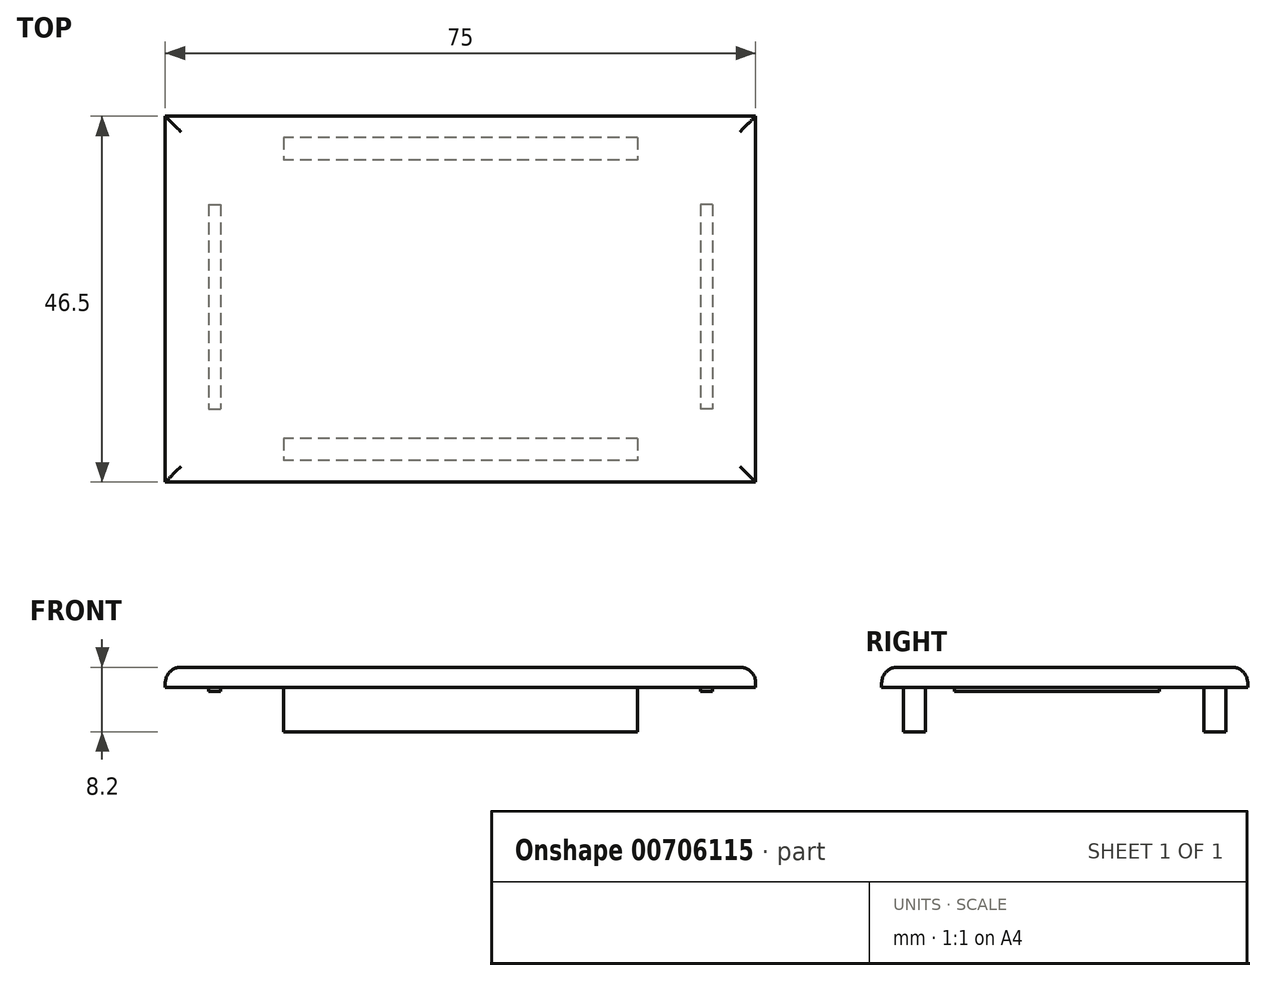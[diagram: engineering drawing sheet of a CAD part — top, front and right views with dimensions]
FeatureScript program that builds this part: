
annotation { "Feature Type Name" : "Feature", "Feature Type Description" : "" }
export const myFeature = defineFeature(function(context is Context, id is Id, definition is map)
    precondition{}
    {
        {
            var Q0;
            Q0=qCreatedBy(makeId("Top.planeOp"),FACE);
            var sketch = newSketch(context, id + "F0", { "sketchPlane" : qUnion([Q0])});
            skLineSegment(sketch, "E0.bottom", {"start": v(37.5, -23.25) * mm, "end": v(-37.5, -23.25) * mm});
            skLineSegment(sketch, "E0.top", {"start": v(37.5, 23.25) * mm, "end": v(-37.5, 23.25) * mm});
            skLineSegment(sketch, "E0.left", {"start": v(37.5, -23.25) * mm, "end": v(37.5, 23.25) * mm});
            skLineSegment(sketch, "E0.right", {"start": v(-37.5, -23.25) * mm, "end": v(-37.5, 23.25) * mm});
            skPoint(sketch, "E0.middle", {"position": v(0, 0) * mm});
            skLineSegment(sketch, "E1.bottom", {"start": v(22.5, 20.5) * mm, "end": v(-22.5, 20.5) * mm});
            skLineSegment(sketch, "E1.top", {"start": v(22.5, -20.5) * mm, "end": v(-22.5, -20.5) * mm});
            skLineSegment(sketch, "E1.left", {"start": v(22.5, 20.5) * mm, "end": v(22.5, -20.5) * mm});
            skLineSegment(sketch, "E1.right", {"start": v(-22.5, 20.5) * mm, "end": v(-22.5, -20.5) * mm});
            skLineSegment(sketch, "E2.0", {"start": v(22.5, -17.7) * mm, "end": v(-22.5, -17.7) * mm});
            skLineSegment(sketch, "E3.0", {"start": v(22.5, 17.7) * mm, "end": v(-22.5, 17.7) * mm});
            skLineSegment(sketch, "E4.bottom", {"start": v(-32, 12.03) * mm, "end": v(-30.5, 12.03) * mm});
            skLineSegment(sketch, "E4.top", {"start": v(-32, -13.98) * mm, "end": v(-30.5, -13.98) * mm});
            skLineSegment(sketch, "E4.left", {"start": v(-32, 12.03) * mm, "end": v(-32, -13.98) * mm});
            skLineSegment(sketch, "E4.right", {"start": v(-30.5, 12.03) * mm, "end": v(-30.5, -13.98) * mm});
            skLineSegment(sketch, "E5.MirrorCS", {"start": v(32, 12.03) * mm, "end": v(30.5, 12.03) * mm});
            skLineSegment(sketch, "E6.MirrorCS", {"start": v(32, 12.03) * mm, "end": v(32, -13.98) * mm});
            skLineSegment(sketch, "E7.MirrorCS", {"start": v(30.5, 12.03) * mm, "end": v(30.5, -13.98) * mm});
            skLineSegment(sketch, "E8.MirrorCS", {"start": v(32, -13.98) * mm, "end": v(30.5, -13.98) * mm});
            skSolve(sketch);
        }
        {
            var Q0;
            Q0=makeQuery(id+"F0.imprint","IMPRINT",FACE,{"disambiguationData":[TD([[makeQuery(id+"F0.imprint","IMPRINT",EDGE,{"derivedFrom":sQuery(id+"F0.wireOp",EDGE,"E0.bottom")}),-1.0]])]});
            var Q1;
            Q1=makeQuery(id+"F0.imprint","IMPRINT",FACE,{"disambiguationData":[TD([[makeQuery(id+"F0.imprint","IMPRINT",EDGE,{"derivedFrom":sQuery(id+"F0.wireOp",EDGE,"E4.bottom")}),-1.0]])]});
            var Q2;
            {var subQ0=sQuery(id+"F0.wireOp",EDGE,"E1.bottom");Q2=makeQuery(id+"F0.imprint","IMPRINT",FACE,{"disambiguationData":[TD([[makeQuery(id+"F0.imprint","IMPRINT",EDGE,{"derivedFrom":subQ0}),1.0]])]});}
            var Q3;
            {var subQ0=sQuery(id+"F0.wireOp",EDGE,"E2.0");Q3=makeQuery(id+"F0.imprint","IMPRINT",FACE,{"disambiguationData":[TD([[makeQuery(id+"F0.imprint","IMPRINT",EDGE,{"derivedFrom":subQ0}),-1.0]])]});}
            var Q4;
            {var subQ0=sQuery(id+"F0.wireOp",EDGE,"E1.top");Q4=makeQuery(id+"F0.imprint","IMPRINT",FACE,{"disambiguationData":[TD([[makeQuery(id+"F0.imprint","IMPRINT",EDGE,{"derivedFrom":subQ0}),-1.0]])]});}
            var Q5;
            Q5=makeQuery(id+"F0.imprint","IMPRINT",FACE,{"disambiguationData":[TD([[makeQuery(id+"F0.imprint","IMPRINT",EDGE,{"derivedFrom":sQuery(id+"F0.wireOp",EDGE,"E5.MirrorCS")}),1.0]])]});
            extrude(context, id + "F1", {"entities" : qUnion([Q0, Q1, Q2, Q3, Q4, Q5]), "depth" : 2.6 * mm, "offsetDistance" : 25 * mm});
        }
        {
            var Q0;
            {var subQ0=sQuery(id+"F0.wireOp",EDGE,"E1.top");Q0=makeQuery(id+"F0.imprint","IMPRINT",FACE,{"disambiguationData":[TD([[makeQuery(id+"F0.imprint","IMPRINT",EDGE,{"derivedFrom":subQ0}),-1.0]])]});}
            var Q1;
            {var subQ0=sQuery(id+"F0.wireOp",EDGE,"E1.bottom");Q1=makeQuery(id+"F0.imprint","IMPRINT",FACE,{"disambiguationData":[TD([[makeQuery(id+"F0.imprint","IMPRINT",EDGE,{"derivedFrom":subQ0}),1.0]])]});}
            extrude(context, id + "F2", {"entities" : qUnion([Q0, Q1]), "oppositeDirection" : true, "depth" : 5.6 * mm, "offsetDistance" : 25 * mm});
        }
        {
            var Q0;
            Q0=makeQuery(id+"F0.imprint","IMPRINT",FACE,{"disambiguationData":[TD([[makeQuery(id+"F0.imprint","IMPRINT",EDGE,{"derivedFrom":sQuery(id+"F0.wireOp",EDGE,"E4.bottom")}),-1.0]])]});
            var Q1;
            Q1=makeQuery(id+"F0.imprint","IMPRINT",FACE,{"disambiguationData":[TD([[makeQuery(id+"F0.imprint","IMPRINT",EDGE,{"derivedFrom":sQuery(id+"F0.wireOp",EDGE,"E5.MirrorCS")}),1.0]])]});
            extrude(context, id + "F3", {"entities" : qUnion([Q0, Q1]), "oppositeDirection" : true, "depth" : .5 * mm, "offsetDistance" : 25 * mm});
        }
        {
            var Q0;
            Q0=makeQuery(id+"F1.opExtrude","CAP_EDGE",EDGE,{"disambiguationData":[OSD([sQuery(id+"F0.wireOp",EDGE,"E0.left")])],"isStart":false});
            var Q1;
            Q1=makeQuery(id+"F1.opExtrude","CAP_EDGE",EDGE,{"disambiguationData":[OSD([sQuery(id+"F0.wireOp",EDGE,"E0.bottom")])],"isStart":false});
            var Q2;
            Q2=makeQuery(id+"F1.opExtrude","CAP_EDGE",EDGE,{"disambiguationData":[OSD([sQuery(id+"F0.wireOp",EDGE,"E0.top")])],"isStart":false});
            var Q3;
            Q3=makeQuery(id+"F1.opExtrude","CAP_EDGE",EDGE,{"disambiguationData":[OSD([sQuery(id+"F0.wireOp",EDGE,"E0.right")])],"isStart":false});
            fillet(context, id + "F4", {"entities" : qUnion([Q0, Q1, Q2, Q3]), "radius" : 2 * mm, "tangentPropagation" : true, "allowEdgeOverflow" : false});
        }
    });
